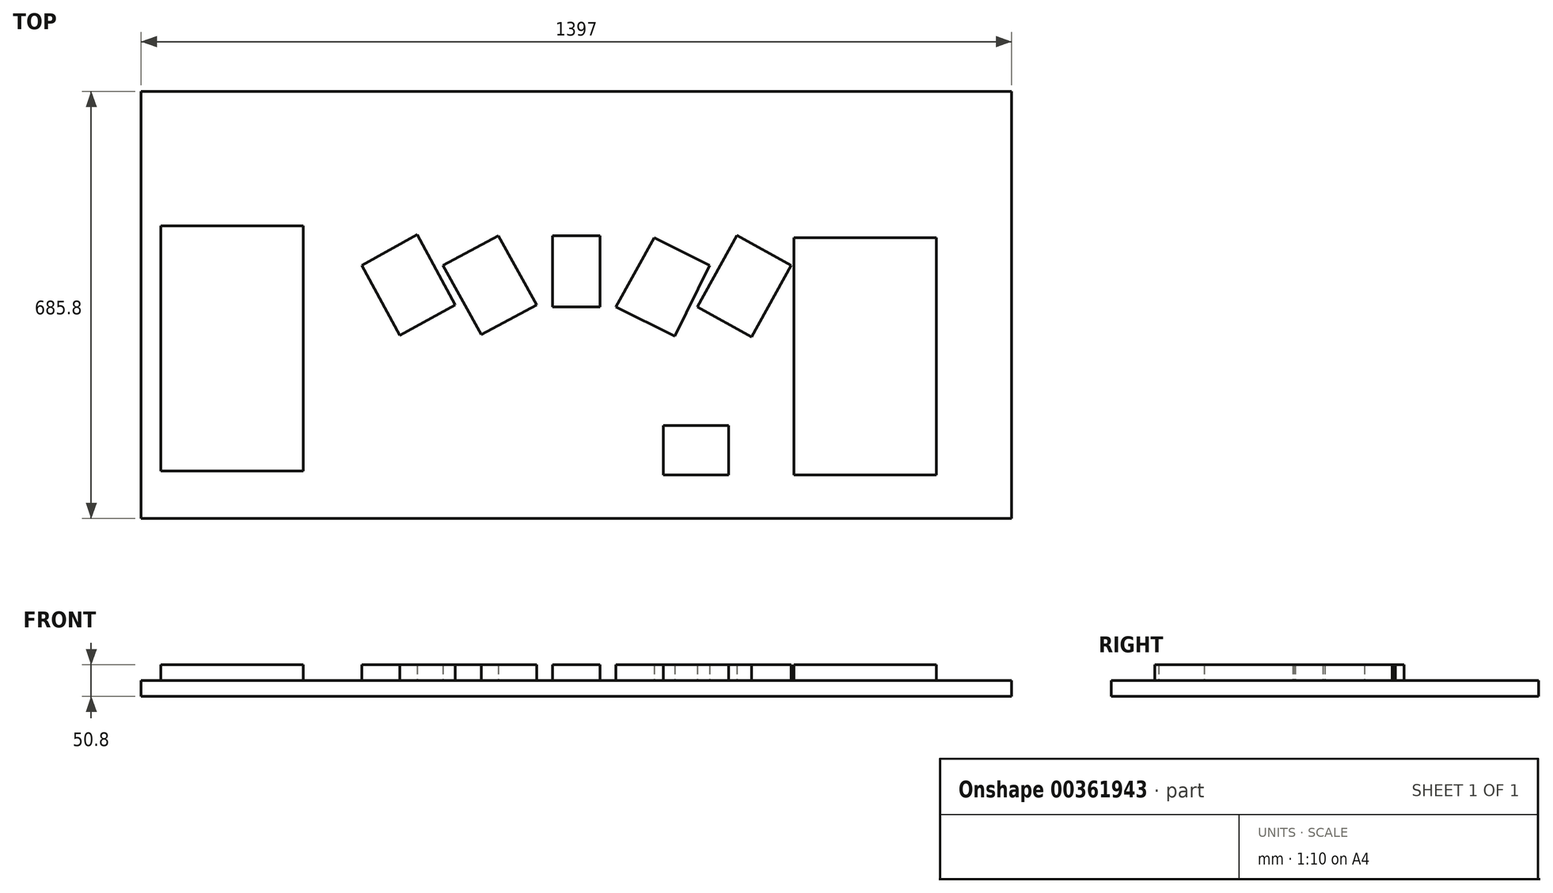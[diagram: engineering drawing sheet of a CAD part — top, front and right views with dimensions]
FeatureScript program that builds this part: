
annotation { "Feature Type Name" : "Feature", "Feature Type Description" : "" }
export const myFeature = defineFeature(function(context is Context, id is Id, definition is map)
    precondition{}
    {
        {
            var Q0;
            Q0=qCreatedBy(makeId("Top.planeOp"),FACE);
            var sketch = newSketch(context, id + "F0", { "sketchPlane" : qUnion([Q0])});
            skLineSegment(sketch, "E0.bottom", {"start": v(698.5, 342.9) * mm, "end": v(-698.5, 342.9) * mm});
            skLineSegment(sketch, "E0.top", {"start": v(698.5, -342.9) * mm, "end": v(-698.5, -342.9) * mm});
            skLineSegment(sketch, "E0.left", {"start": v(698.5, 342.9) * mm, "end": v(698.5, -342.9) * mm});
            skLineSegment(sketch, "E0.right", {"start": v(-698.5, 342.9) * mm, "end": v(-698.5, -342.9) * mm});
            skPoint(sketch, "E0.middle", {"position": v(0, 0) * mm});
            skSolve(sketch);
        }
        {
            var Q0;
            Q0=qSketchRegion(id+"F0",true);
            extrude(context, id + "F1", {"entities" : qUnion([Q0]), "depth" : 25.4 * mm});
        }
        {
            var Q0;
            Q0=makeQuery(id+"F1.opExtrude","CAP_FACE",FACE,{"disambiguationData":[OSD([sQuery(id+"F0.wireOp",EDGE,"E0.bottom"),sQuery(id+"F0.wireOp",EDGE,"E0.top"),sQuery(id+"F0.wireOp",EDGE,"E0.left"),sQuery(id+"F0.wireOp",EDGE,"E0.right")])],"isStart":false});
            var sketch = newSketch(context, id + "F2", { "sketchPlane" : qUnion([Q0])});
            skLineSegment(sketch, "E1.bottom", {"start": v(241.3, -143.2) * mm, "end": v(-393.7, -143.2) * mm, "construction": true});
            skLineSegment(sketch, "E1.top", {"start": v(241.3, -67) * mm, "end": v(-393.7, -67) * mm, "construction": true});
            skLineSegment(sketch, "E1.left", {"start": v(241.3, -143.2) * mm, "end": v(241.3, -67) * mm, "construction": true});
            skLineSegment(sketch, "E1.right", {"start": v(-393.7, -143.2) * mm, "end": v(-393.7, -67) * mm, "construction": true});
            skPoint(sketch, "E1.middle", {"position": v(-76.2, -105.1) * mm});
            skLineSegment(sketch, "E2.bottom", {"start": v(-38.1, -3.42) * mm, "end": v(38.1, -3.56) * mm});
            skLineSegment(sketch, "E2.left", {"start": v(-38.1, -3.42) * mm, "end": v(-38.1, 110.74) * mm});
            skLineSegment(sketch, "E2.right", {"start": v(38.1, -3.56) * mm, "end": v(38.1, 110.74) * mm});
            skLineSegment(sketch, "E3", {"start": v(38.1, 110.74) * mm, "end": v(-38.1, 110.74) * mm});
            skPoint(sketch, "E4", {"position": v(-3.46, -67) * mm});
            skPoint(sketch, "E5.positionSnap0", {"position": v(241.3, -105.1) * mm});
            skPoint(sketch, "E6", {"position": v(-438.15, 127) * mm});
            skLineSegment(sketch, "E7.bottom", {"start": v(-438.15, 127) * mm, "end": v(-666.75, 127) * mm});
            skLineSegment(sketch, "E7.top", {"start": v(-438.15, -266.7) * mm, "end": v(-666.75, -266.7) * mm});
            skLineSegment(sketch, "E7.left", {"start": v(-438.15, 127) * mm, "end": v(-438.15, -266.7) * mm});
            skLineSegment(sketch, "E7.right", {"start": v(-666.75, 127) * mm, "end": v(-666.75, -266.7) * mm});
            skLineSegment(sketch, "E8.bottom", {"start": v(349.25, 107.95) * mm, "end": v(577.85, 107.95) * mm});
            skLineSegment(sketch, "E8.top", {"start": v(349.25, -273.05) * mm, "end": v(577.85, -273.05) * mm});
            skLineSegment(sketch, "E8.left", {"start": v(349.25, 107.95) * mm, "end": v(349.25, -273.05) * mm});
            skLineSegment(sketch, "E8.right", {"start": v(577.85, 107.95) * mm, "end": v(577.85, -273.05) * mm});
            skLineSegment(sketch, "E9.top", {"start": v(139.7, -193.64) * mm, "end": v(244.2, -193.64) * mm});
            skLineSegment(sketch, "E9.left", {"start": v(139.7, -273.05) * mm, "end": v(139.7, -193.64) * mm});
            skLineSegment(sketch, "E9.right", {"start": v(244.2, -273.05) * mm, "end": v(244.2, -193.64) * mm});
            skLineSegment(sketch, "E10", {"start": v(139.7, -273.05) * mm, "end": v(244.2, -273.05) * mm});
            skLineSegment(sketch, "E11", {"start": v(63.5, -3.56) * mm, "end": v(157.79, -50.21) * mm});
            skLineSegment(sketch, "E12", {"start": v(157.79, -50.21) * mm, "end": v(214.04, 63.5) * mm});
            skLineSegment(sketch, "E13", {"start": v(214.04, 63.5) * mm, "end": v(124.98, 107.56) * mm});
            skLineSegment(sketch, "E14", {"start": v(124.98, 107.56) * mm, "end": v(63.5, -3.56) * mm});
            skLineSegment(sketch, "E15", {"start": v(194.13, -3.56) * mm, "end": v(280.86, -51.55) * mm});
            skLineSegment(sketch, "E16", {"start": v(280.86, -51.55) * mm, "end": v(344.51, 63.5) * mm});
            skLineSegment(sketch, "E17", {"start": v(344.51, 63.5) * mm, "end": v(257.78, 111.49) * mm});
            skLineSegment(sketch, "E18", {"start": v(257.78, 111.49) * mm, "end": v(194.13, -3.56) * mm});
            skPoint(sketch, "E19.endSnap0", {"position": v(0, 342.9) * mm});
            skLineSegment(sketch, "E20.MirrorCS", {"start": v(-124.98, 111.13) * mm, "end": v(-63.5, 0) * mm});
            skLineSegment(sketch, "E21.MirrorCS", {"start": v(-213.88, 63.5) * mm, "end": v(-124.98, 111.13) * mm});
            skLineSegment(sketch, "E22.MirrorCS", {"start": v(-63.5, 0) * mm, "end": v(-152.4, -47.63) * mm});
            skLineSegment(sketch, "E23.MirrorCS", {"start": v(-152.4, -47.63) * mm, "end": v(-213.88, 63.5) * mm});
            skLineSegment(sketch, "E24.MirrorCS", {"start": v(-255.61, 112.69) * mm, "end": v(-194.13, 0) * mm});
            skLineSegment(sketch, "E25.MirrorCS", {"start": v(-194.13, 0) * mm, "end": v(-283.03, -49.19) * mm});
            skLineSegment(sketch, "E26.MirrorCS", {"start": v(-283.03, -49.19) * mm, "end": v(-344.51, 63.5) * mm});
            skLineSegment(sketch, "E27.MirrorCS", {"start": v(-344.51, 63.5) * mm, "end": v(-255.61, 112.69) * mm});
            skPoint(sketch, "E28", {"position": v(110.64, -26.89) * mm});
            skPoint(sketch, "E29", {"position": v(-107.95, -23.81) * mm});
            skPoint(sketch, "E30", {"position": v(-238.58, -24.6) * mm});
            skPoint(sketch, "E31", {"position": v(237.5, -27.55) * mm});
            skPoint(sketch, "E32", {"position": v(-438.15, -69.85) * mm});
            skPoint(sketch, "E33", {"position": v(349.25, -82.55) * mm});
            skPoint(sketch, "E34", {"position": v(191.95, -233.35) * mm});
            skPoint(sketch, "E34.positionSnap0", {"position": v(191.95, -193.64) * mm});
            skPoint(sketch, "E34.positionSnap1", {"position": v(139.7, -233.35) * mm});
            skSolve(sketch);
        }
        {
            var Q0;
            Q0=qSketchRegion(id+"F2",true);
            extrude(context, id + "F3", {"entities" : qUnion([Q0]), "depth" : 25.4 * mm});
        }
    });
